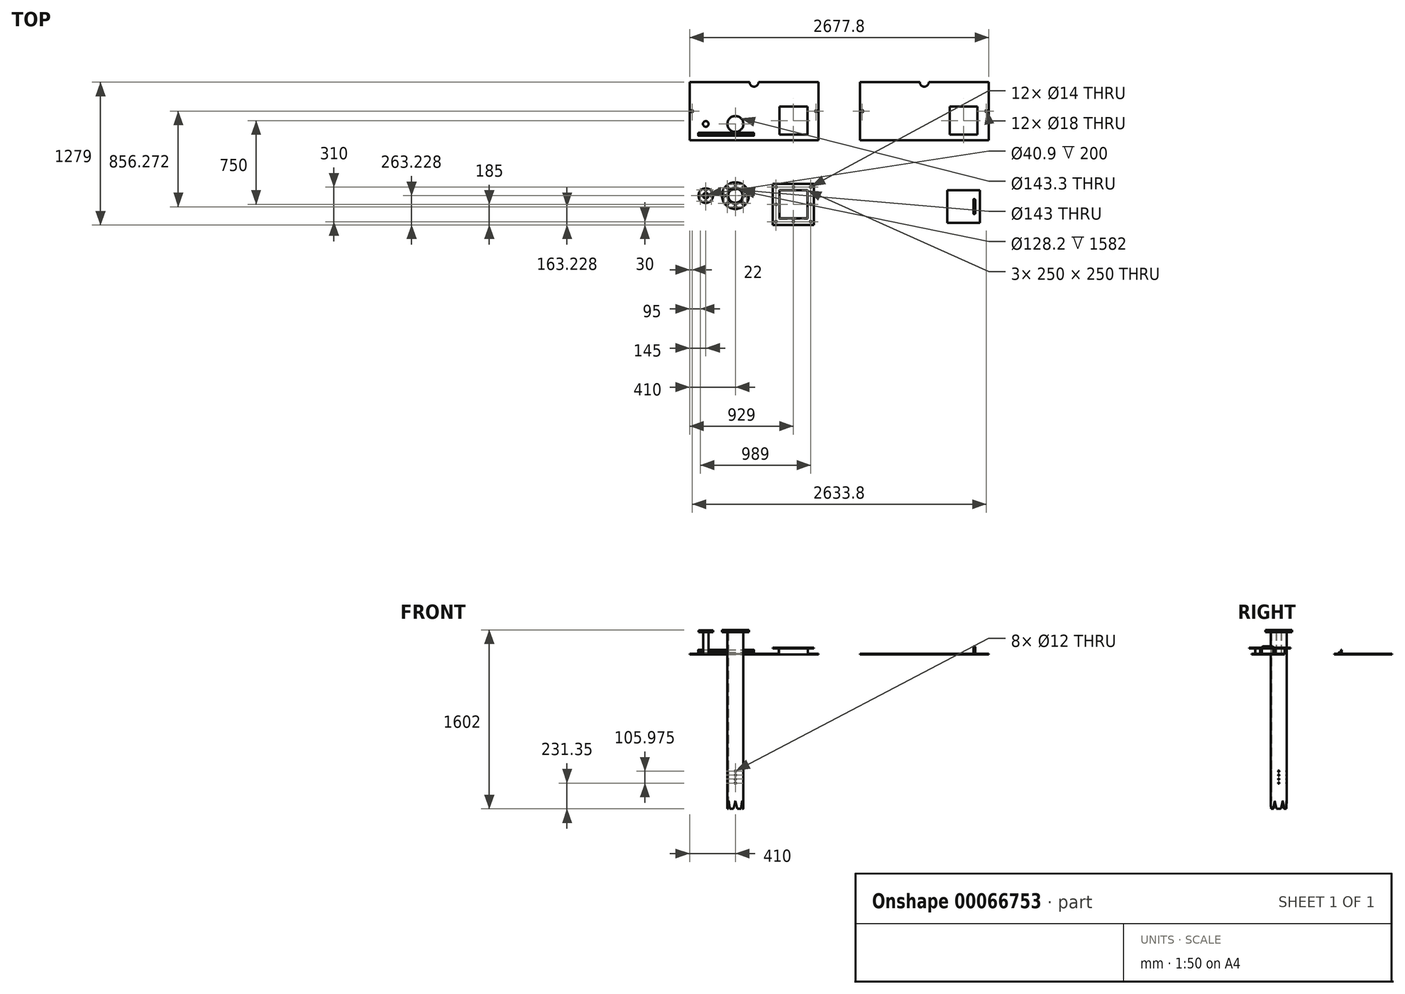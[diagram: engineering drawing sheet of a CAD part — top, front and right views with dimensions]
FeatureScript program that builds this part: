
annotation { "Feature Type Name" : "Feature", "Feature Type Description" : "" }
export const myFeature = defineFeature(function(context is Context, id is Id, definition is map)
    precondition{}
    {
        {
            assignVariable(context, id + "F0", {"name" : "C3", "anyValue" : 6});
        }
        {
            assignVariable(context, id + "F1", {"name" : "C5", "anyValue" : 250});
        }
        {
            assignVariable(context, id + "F2", {"name" : "C7", "anyValue" : 60});
        }
        {
            assignVariable(context, id + "F3", {"name" : "C8", "anyValue" : 6});
        }
        {
            assignVariable(context, id + "F4", {"name" : "C14", "anyValue" : 16});
        }
        {
            assignVariable(context, id + "F5", {"name" : "C16", "anyValue" : 4});
        }
        {
            assignVariable(context, id + "F6", {"name" : "C23", "anyValue" : 20});
        }
        {
            assignVariable(context, id + "F7", {"name" : "C25", "anyValue" : 8});
        }
        {
            var Q0;
            Q0=qCreatedBy(makeId("Top.planeOp"),FACE);
            var sketch = newSketch(context, id + "F8", { "sketchPlane" : qUnion([Q0])});
            skLineSegment(sketch, "E0.bottom", {"start": v(-577, 0) * mm, "end": v(-40, 0) * mm});
            skLineSegment(sketch, "E0.top", {"start": v(-577, -519) * mm, "end": v(577, -519) * mm});
            skLineSegment(sketch, "E0.left", {"start": v(-577, 0) * mm, "end": v(-577, -519) * mm});
            skLineSegment(sketch, "E0.right", {"start": v(577, 0) * mm, "end": v(577, -519) * mm});
            skArc(sketch, "E1", {"start": v(-40, 0) * mm, "mid": v(0, -40) * mm, "end": v(40, 0) * mm});
            skLineSegment(sketch, "E2.trimOffspring", {"start": v(40, 0) * mm, "end": v(577, 0) * mm});
            skCircle(sketch, "E3", {"center": v(-432, -374.1) * mm, "radius": 25.15 * mm});
            skCircle(sketch, "E4", {"center": v(-167, -374.1) * mm, "radius": 71.65 * mm});
            skLineSegment(sketch, "E5.bottom", {"start": v(227, -219) * mm, "end": v(477, -219) * mm});
            skLineSegment(sketch, "E5.top", {"start": v(227, -469) * mm, "end": v(477, -469) * mm});
            skLineSegment(sketch, "E5.left", {"start": v(227, -219) * mm, "end": v(227, -469) * mm});
            skLineSegment(sketch, "E5.right", {"start": v(477, -219) * mm, "end": v(477, -469) * mm});
            skLineSegment(sketch, "E6.bottom", {"start": v(946.8, 0) * mm, "end": v(1483.8, 0) * mm});
            skLineSegment(sketch, "E6.top", {"start": v(946.8, -519) * mm, "end": v(2100.8, -519) * mm});
            skLineSegment(sketch, "E6.left", {"start": v(946.8, 0) * mm, "end": v(946.8, -519) * mm});
            skLineSegment(sketch, "E6.right", {"start": v(2100.8, 0) * mm, "end": v(2100.8, -519) * mm});
            skArc(sketch, "E7", {"start": v(1483.8, 0) * mm, "mid": v(1523.8, -40) * mm, "end": v(1563.8, 0) * mm});
            skLineSegment(sketch, "E8.trimOffspring", {"start": v(1563.8, 0) * mm, "end": v(2100.8, 0) * mm});
            skLineSegment(sketch, "E9.bottom", {"start": v(1750.8, -219) * mm, "end": v(2000.8, -219) * mm});
            skLineSegment(sketch, "E9.top", {"start": v(1750.8, -469) * mm, "end": v(2000.8, -469) * mm});
            skLineSegment(sketch, "E9.left", {"start": v(1750.8, -219) * mm, "end": v(1750.8, -469) * mm});
            skLineSegment(sketch, "E9.right", {"start": v(2000.8, -219) * mm, "end": v(2000.8, -469) * mm});
            skLineSegment(sketch, "E10.bottom", {"start": v(227, -969) * mm, "end": v(477, -969) * mm});
            skLineSegment(sketch, "E10.top", {"start": v(227, -1219) * mm, "end": v(477, -1219) * mm});
            skLineSegment(sketch, "E10.left", {"start": v(227, -969) * mm, "end": v(227, -1219) * mm});
            skLineSegment(sketch, "E10.right", {"start": v(477, -969) * mm, "end": v(477, -1219) * mm});
            skLineSegment(sketch, "E11.bottom", {"start": v(221, -963) * mm, "end": v(483, -963) * mm});
            skLineSegment(sketch, "E11.top", {"start": v(221, -1225) * mm, "end": v(483, -1225) * mm});
            skLineSegment(sketch, "E11.left", {"start": v(221, -963) * mm, "end": v(221, -1225) * mm});
            skLineSegment(sketch, "E11.right", {"start": v(483, -963) * mm, "end": v(483, -1225) * mm});
            skLineSegment(sketch, "E12", {"start": v(352, -469) * mm, "end": v(352, -963) * mm, "construction": true});
            skLineSegment(sketch, "E13", {"start": v(-432, -374.1) * mm, "end": v(-432, -1015.77) * mm, "construction": true});
            skCircle(sketch, "E14", {"center": v(-432, -1015.77) * mm, "radius": 20.45 * mm});
            skCircle(sketch, "E15", {"center": v(-432, -1015.77) * mm, "radius": 24.15 * mm});
            skLineSegment(sketch, "E16", {"start": v(-167, -374.1) * mm, "end": v(-167, -1015.77) * mm, "construction": true});
            skCircle(sketch, "E17", {"center": v(-167, -1015.77) * mm, "radius": 64.1 * mm});
            skCircle(sketch, "E18", {"center": v(-167, -1015.77) * mm, "radius": 70.65 * mm});
            skLineSegment(sketch, "E19", {"start": v(1875.8, -469) * mm, "end": v(1875.8, -969) * mm, "construction": true});
            skLineSegment(sketch, "E20.bottom", {"start": v(1730.8, -969) * mm, "end": v(2020.8, -969) * mm});
            skLineSegment(sketch, "E20.top", {"start": v(1730.8, -1259) * mm, "end": v(2020.8, -1259) * mm});
            skLineSegment(sketch, "E20.left", {"start": v(1730.8, -969) * mm, "end": v(1730.8, -1259) * mm});
            skLineSegment(sketch, "E20.right", {"start": v(2020.8, -969) * mm, "end": v(2020.8, -1259) * mm});
            skCircle(sketch, "E21", {"center": v(555, -259.5) * mm, "radius": 9 * mm});
            skLineSegment(sketch, "E22", {"start": v(555, -259.5) * mm, "end": v(577, -259.5) * mm, "construction": true});
            skCircle(sketch, "E23.MirrorC", {"center": v(-555, -259.5) * mm, "radius": 9 * mm});
            skLineSegment(sketch, "E24", {"start": v(946.8, -259.5) * mm, "end": v(968.8, -259.5) * mm, "construction": true});
            skCircle(sketch, "E25", {"center": v(968.8, -259.5) * mm, "radius": 9 * mm});
            skLineSegment(sketch, "E26", {"start": v(1523.8, 0) * mm, "end": v(1523.8, -89.88) * mm, "construction": true});
            skCircle(sketch, "E27.MirrorC", {"center": v(2078.8, -259.5) * mm, "radius": 9 * mm});
            skSolve(sketch);
        }
        {
            var Q0;
            Q0=makeQuery(id+"F8.imprint","IMPRINT",FACE,{"disambiguationData":[TD([[makeQuery(id+"F8.imprint","IMPRINT",EDGE,{"derivedFrom":sQuery(id+"F8.wireOp",EDGE,"E0.bottom")}),-1.0]])]});
            extrude(context, id + "F9", {"entities" : qUnion([Q0]), "depth" : (getVariable(context, 'C3')) * mm});
        }
        {
            var Q0;
            Q0=makeQuery(id+"F8.imprint","IMPRINT",FACE,{"disambiguationData":[TD([[makeQuery(id+"F8.imprint","IMPRINT",EDGE,{"derivedFrom":sQuery(id+"F8.wireOp",EDGE,"E10.bottom")}),1.0]])]});
            extrude(context, id + "F10", {"entities" : qUnion([Q0]), "depth" : (getVariable(context, 'C7')) * mm});
        }
        {
            var Q0;
            Q0=makeQuery(id+"F10.opExtrude","CAP_FACE",FACE,{"disambiguationData":[OSD([sQuery(id+"F8.wireOp",EDGE,"E10.bottom"),sQuery(id+"F8.wireOp",EDGE,"E10.top"),sQuery(id+"F8.wireOp",EDGE,"E10.left"),sQuery(id+"F8.wireOp",EDGE,"E10.right"),sQuery(id+"F8.wireOp",EDGE,"E11.bottom"),sQuery(id+"F8.wireOp",EDGE,"E11.top"),sQuery(id+"F8.wireOp",EDGE,"E11.left"),sQuery(id+"F8.wireOp",EDGE,"E11.right")])],"isStart":false});
            var sketch = newSketch(context, id + "F11", { "sketchPlane" : qUnion([Q0])});
            skLineSegment(sketch, "E28.bottom", {"start": v(167, -909) * mm, "end": v(537, -909) * mm});
            skLineSegment(sketch, "E28.top", {"start": v(167, -1279) * mm, "end": v(537, -1279) * mm});
            skLineSegment(sketch, "E28.left", {"start": v(167, -909) * mm, "end": v(167, -1279) * mm});
            skLineSegment(sketch, "E28.right", {"start": v(537, -909) * mm, "end": v(537, -1279) * mm});
            skLineSegment(sketch, "E29.bottom", {"start": v(227, -969) * mm, "end": v(477, -969) * mm});
            skLineSegment(sketch, "E29.top", {"start": v(227, -1219) * mm, "end": v(477, -1219) * mm});
            skLineSegment(sketch, "E29.left", {"start": v(227, -969) * mm, "end": v(227, -1219) * mm});
            skLineSegment(sketch, "E29.right", {"start": v(477, -969) * mm, "end": v(477, -1219) * mm});
            skLineSegment(sketch, "E30.bottom", {"start": v(197, -939) * mm, "end": v(507, -939) * mm, "construction": true});
            skLineSegment(sketch, "E30.top", {"start": v(197, -1249) * mm, "end": v(507, -1249) * mm, "construction": true});
            skLineSegment(sketch, "E30.left", {"start": v(197, -939) * mm, "end": v(197, -1249) * mm, "construction": true});
            skLineSegment(sketch, "E30.right", {"start": v(507, -939) * mm, "end": v(507, -1249) * mm, "construction": true});
            skCircle(sketch, "E31", {"center": v(197, -939) * mm, "radius": 7 * mm});
            skCircle(sketch, "E32", {"center": v(507, -939) * mm, "radius": 7 * mm});
            skCircle(sketch, "E33", {"center": v(352, -939) * mm, "radius": 7 * mm});
            skCircle(sketch, "E34", {"center": v(197, -1094) * mm, "radius": 7 * mm});
            skCircle(sketch, "E35", {"center": v(197, -1249) * mm, "radius": 7 * mm});
            skCircle(sketch, "E36", {"center": v(352, -1249) * mm, "radius": 7 * mm});
            skCircle(sketch, "E37", {"center": v(507, -1249) * mm, "radius": 7 * mm});
            skCircle(sketch, "E38", {"center": v(507, -1094) * mm, "radius": 7 * mm});
            skSolve(sketch);
        }
        {
            var Q0;
            Q0=makeQuery(id+"F11.imprint","IMPRINT",FACE,{"disambiguationData":[TD([[makeQuery(id+"F11.imprint","IMPRINT",EDGE,{"derivedFrom":sQuery(id+"F11.wireOp",EDGE,"E28.bottom")}),-1.0]])]});
            extrude(context, id + "F12", {"entities" : qUnion([Q0]), "operationType" : NewBodyOperationType.ADD, "oppositeDirection" : true, "depth" : (getVariable(context, 'C8')) * mm});
        }
        {
            var Q0;
            Q0=makeQuery(id+"F8.imprint","IMPRINT",FACE,{"disambiguationData":[TD([[makeQuery(id+"F8.imprint","IMPRINT",EDGE,{"derivedFrom":sQuery(id+"F8.wireOp",EDGE,"E14")}),-1.0]])]});
            extrude(context, id + "F13", {"entities" : qUnion([Q0]), "depth" : 200 * mm});
        }
        {
            var Q0;
            Q0=makeQuery(id+"F13.opExtrude","CAP_FACE",FACE,{"disambiguationData":[OSD([sQuery(id+"F8.wireOp",EDGE,"E14"),sQuery(id+"F8.wireOp",EDGE,"E15")])],"isStart":false});
            var sketch = newSketch(context, id + "F14", { "sketchPlane" : qUnion([Q0])});
            skCircle(sketch, "E39", {"center": v(-432, -1015.77) * mm, "radius": 24.75 * mm});
            skCircle(sketch, "E40", {"center": v(-432, -1015.77) * mm, "radius": 65 * mm});
            skCircle(sketch, "E41", {"center": v(-432, -1015.77) * mm, "radius": 50 * mm, "construction": true});
            skCircle(sketch, "E42", {"center": v(-432, -965.77) * mm, "radius": 7 * mm});
            skSolve(sketch);
        }
        {
            var Q0;
            Q0=makeQuery(id+"F14.imprint","IMPRINT",FACE,{"disambiguationData":[TD([[makeQuery(id+"F14.imprint","IMPRINT",EDGE,{"derivedFrom":sQuery(id+"F14.wireOp",EDGE,"E39")}),-1.0]])]});
            extrude(context, id + "F15", {"entities" : qUnion([Q0]), "depth" : (getVariable(context, 'C14')) * mm});
        }
        {
            var Q0;
            Q0=makeQuery(id+"F15.opExtrude","SWEPT_FACE",FACE,{"disambiguationData":[OSD([sQuery(id+"F14.wireOp",EDGE,"E42")])]});
            var Q1;
            Q1=makeQuery(id+"F15.opExtrude","CAP_EDGE",EDGE,{"disambiguationData":[OSD([sQuery(id+"F14.wireOp",EDGE,"E39")])],"isStart":false});
            circularPattern(context, id + "F16", {"faces" : qUnion([Q0]), "axis" : qUnion([Q1]), "angle" : 360 * degree, "instanceCount" : getVariable(context, 'C16'), "equalSpace" : true, "patternType" : PatternType.FACE});
        }
        {
            assignVariable(context, id + "F17", {"name" : "C29", "anyValue" : 1382});
        }
        {
            var Q0;
            Q0=makeQuery(id+"F8.imprint","IMPRINT",FACE,{"disambiguationData":[TD([[makeQuery(id+"F8.imprint","IMPRINT",EDGE,{"derivedFrom":sQuery(id+"F8.wireOp",EDGE,"E17")}),-1.0]])]});
            extrude(context, id + "F18", {"entities" : qUnion([Q0]), "depth" : 200 * mm, "hasSecondDirection" : true, "secondDirectionOppositeDirection" : true, "secondDirectionDepth" : (getVariable(context, 'C29')) * mm});
        }
        {
            var Q0;
            Q0=makeQuery(id+"F18.opExtrude","CAP_FACE",FACE,{"disambiguationData":[OSD([sQuery(id+"F8.wireOp",EDGE,"E17"),sQuery(id+"F8.wireOp",EDGE,"E18")])],"isStart":false});
            var sketch = newSketch(context, id + "F19", { "sketchPlane" : qUnion([Q0])});
            skCircle(sketch, "E43", {"center": v(-167, -1015.77) * mm, "radius": 71.5 * mm});
            skCircle(sketch, "E44", {"center": v(-167, -1015.77) * mm, "radius": 120 * mm});
            skCircle(sketch, "E45", {"center": v(-167, -1015.77) * mm, "radius": 100 * mm, "construction": true});
            skCircle(sketch, "E46", {"center": v(-167, -915.77) * mm, "radius": 9 * mm});
            skSolve(sketch);
        }
        {
            var Q0;
            Q0=makeQuery(id+"F19.imprint","IMPRINT",FACE,{"disambiguationData":[TD([[makeQuery(id+"F19.imprint","IMPRINT",EDGE,{"derivedFrom":sQuery(id+"F19.wireOp",EDGE,"E43")}),-1.0]])]});
            extrude(context, id + "F20", {"entities" : qUnion([Q0]), "depth" : (getVariable(context, 'C23')) * mm});
        }
        {
            var Q0;
            Q0=makeQuery(id+"F20.opExtrude","SWEPT_FACE",FACE,{"disambiguationData":[OSD([sQuery(id+"F19.wireOp",EDGE,"E46")])]});
            var Q1;
            Q1=makeQuery(id+"F20.opExtrude","CAP_EDGE",EDGE,{"disambiguationData":[OSD([sQuery(id+"F19.wireOp",EDGE,"E43")])],"isStart":false});
            circularPattern(context, id + "F21", {"faces" : qUnion([Q0]), "axis" : qUnion([Q1]), "angle" : 360 * degree, "instanceCount" : getVariable(context, 'C25'), "equalSpace" : true, "patternType" : PatternType.FACE});
        }
        {
            var Q0;
            Q0=makeQuery(id+"F8.imprint","IMPRINT",FACE,{"disambiguationData":[TD([[makeQuery(id+"F8.imprint","IMPRINT",EDGE,{"derivedFrom":sQuery(id+"F8.wireOp",EDGE,"E6.bottom")}),-1.0]])]});
            extrude(context, id + "F22", {"entities" : qUnion([Q0]), "depth" : (getVariable(context, 'C3')) * mm});
        }
        {
            var Q0;
            Q0=makeQuery(id+"F8.imprint","IMPRINT",FACE,{"disambiguationData":[TD([[makeQuery(id+"F8.imprint","IMPRINT",EDGE,{"derivedFrom":sQuery(id+"F8.wireOp",EDGE,"E20.bottom")}),-1.0]])]});
            extrude(context, id + "F23", {"entities" : qUnion([Q0]), "depth" : (getVariable(context, 'C8')) * mm});
        }
        {
            var Q0;
            Q0=qCreatedBy(makeId("Right.planeOp"),FACE);
            var sketch = newSketch(context, id + "F24", { "sketchPlane" : qUnion([Q0])});
            skLineSegment(sketch, "E47", {"start": v(-478.36, 15.27) * mm, "end": v(-453.36, 15.27) * mm});
            skLineSegment(sketch, "E48", {"start": v(-453.36, 15.27) * mm, "end": v(-453.36, 40.27) * mm});
            skLineSegment(sketch, "E49", {"start": v(-453.36, 40.27) * mm, "end": v(-456.36, 40.27) * mm});
            skLineSegment(sketch, "E50", {"start": v(-458.36, 38.27) * mm, "end": v(-458.36, 23.77) * mm});
            skLineSegment(sketch, "E51", {"start": v(-461.86, 20.27) * mm, "end": v(-476.36, 20.27) * mm});
            skLineSegment(sketch, "E52", {"start": v(-478.36, 18.27) * mm, "end": v(-478.36, 15.27) * mm});
            skPoint(sketch, "E53.visualSharp", {"position": v(-458.36, 20.27) * mm});
            skArc(sketch, "E53.filletArc", {"start": v(-461.86, 20.27) * mm, "mid": v(-459.38, 21.3) * mm, "end": v(-458.36, 23.77) * mm});
            skPoint(sketch, "E54.visualSharp", {"position": v(-458.36, 40.27) * mm});
            skArc(sketch, "E54.filletArc", {"start": v(-456.36, 40.27) * mm, "mid": v(-457.77, 39.69) * mm, "end": v(-458.36, 38.27) * mm});
            skPoint(sketch, "E55.visualSharp", {"position": v(-478.36, 20.27) * mm});
            skArc(sketch, "E55.filletArc", {"start": v(-476.36, 20.27) * mm, "mid": v(-477.77, 19.69) * mm, "end": v(-478.36, 18.27) * mm});
            skSolve(sketch);
        }
        {
            var Q0;
            Q0=makeQuery(id+"F24.imprint","IMPRINT",FACE,{"disambiguationData":[TD([[makeQuery(id+"F24.imprint","IMPRINT",EDGE,{"derivedFrom":sQuery(id+"F24.wireOp",EDGE,"E47")}),1.0]])]});
            extrude(context, id + "F25", {"entities" : qUnion([Q0]), "oppositeDirection" : true, "depth" : (2 * getVariable(context, 'C5')) * mm});
        }
        {
            var Q0;
            Q0=makeQuery(id+"F23.opExtrude","CAP_FACE",FACE,{"disambiguationData":[OSD([sQuery(id+"F8.wireOp",EDGE,"E20.bottom"),sQuery(id+"F8.wireOp",EDGE,"E20.top"),sQuery(id+"F8.wireOp",EDGE,"E20.left"),sQuery(id+"F8.wireOp",EDGE,"E20.right")])],"isStart":false});
            var sketch = newSketch(context, id + "F26", { "sketchPlane" : qUnion([Q0])});
            skCircle(sketch, "E56", {"center": v(1970.8, -1174) * mm, "radius": 8 * mm});
            skLineSegment(sketch, "E57", {"start": v(2020.8, -1114) * mm, "end": v(1796.76, -1114) * mm, "construction": true});
            skLineSegment(sketch, "E58", {"start": v(1970.8, -1174) * mm, "end": v(2020.8, -1174) * mm, "construction": true});
            skSolve(sketch);
        }
        {
            var Q0;
            Q0=makeQuery(id+"F23.opExtrude","SWEPT_FACE",FACE,{"disambiguationData":[OSD([sQuery(id+"F8.wireOp",EDGE,"E20.right")])]});
            var sketch = newSketch(context, id + "F27", { "sketchPlane" : qUnion([Q0])});
            skLineSegment(sketch, "E59", {"start": v(-1174, 6) * mm, "end": v(-1174, 36) * mm});
            skLineSegment(sketch, "E60", {"start": v(-1144, 66) * mm, "end": v(-1084, 66) * mm});
            skLineSegment(sketch, "E61", {"start": v(-1054, 36) * mm, "end": v(-1054, 6) * mm});
            skPoint(sketch, "E62.visualSharp", {"position": v(-1174, 66) * mm});
            skArc(sketch, "E62.filletArc", {"start": v(-1144, 66) * mm, "mid": v(-1165.21, 57.21) * mm, "end": v(-1174, 36) * mm});
            skPoint(sketch, "E63.visualSharp", {"position": v(-1054, 66) * mm});
            skArc(sketch, "E63.filletArc", {"start": v(-1054, 36) * mm, "mid": v(-1062.79, 57.21) * mm, "end": v(-1084, 66) * mm});
            skSolve(sketch);
        }
        {
            var Q0;
            Q0=makeQuery(id+"F26.imprint","IMPRINT",FACE,{"disambiguationData":[TD([[makeQuery(id+"F26.imprint","IMPRINT",EDGE,{"derivedFrom":sQuery(id+"F26.wireOp",EDGE,"E56")}),1.0]])]});
            var Q1;
            Q1=sQuery(id+"F27.wireOp",EDGE,"E59");
            var Q2;
            Q2=sQuery(id+"F27.wireOp",EDGE,"E62.filletArc");
            var Q3;
            Q3=sQuery(id+"F27.wireOp",EDGE,"E60");
            var Q4;
            Q4=sQuery(id+"F27.wireOp",EDGE,"E63.filletArc");
            var Q5;
            Q5=sQuery(id+"F27.wireOp",EDGE,"E61");
            sweep(context, id + "F28", {"operationType" : NewBodyOperationType.ADD, "profiles" : qUnion([Q0]), "path" : qUnion([Q1, Q2, Q3, Q4, Q5])});
        }
        {
            var Q0;
            Q0=sQuery(id+"F8.wireOp",VERTEX,"E18.center");
            var Q1;
            Q1=sQuery(id+"F8.wireOp",EDGE,"E16");
            cPlane(context, id + "F29", {"entities" : qUnion([Q0, Q1]), "cplaneType" : CPlaneType.LINE_POINT, "offset" : 150 * mm, "width" : 150 * mm, "height" : 150 * mm});
        }
        {
            assignVariable(context, id + "F30", {"name" : "C28", "anyValue" : 4});
        }
        {
            var Q0;
            Q0=qCreatedBy(id+"F29.planeOp",FACE);
            var sketch = newSketch(context, id + "F31", { "sketchPlane" : qUnion([Q0])});
            skLineSegment(sketch, "E64", {"start": v(-184.66, -1382) * mm, "end": v(-167, -1311.35) * mm});
            skLineSegment(sketch, "E65", {"start": v(-167, -1311.35) * mm, "end": v(-149.34, -1382) * mm});
            skLineSegment(sketch, "E66", {"start": v(-149.34, -1382) * mm, "end": v(-184.66, -1382) * mm});
            skCircle(sketch, "E67", {"center": v(-167, -1150.65) * mm, "radius": 6 * mm});
            skCircle(sketch, "E68", {"center": v(-167, -1115.33) * mm, "radius": 6 * mm});
            skLineSegment(sketch, "E69", {"start": v(-167, -1150.65) * mm, "end": v(-167, -1115.33) * mm, "construction": true});
            skLineSegment(sketch, "E70", {"start": v(-167, -1115.33) * mm, "end": v(-167, -1080) * mm, "construction": true});
            skLineSegment(sketch, "E71", {"start": v(-167, -1080) * mm, "end": v(-167, -1044.67) * mm, "construction": true});
            skLineSegment(sketch, "E72.trimOffspring", {"start": v(-167, -1311.35) * mm, "end": v(-167, -1382) * mm, "construction": true});
            skCircle(sketch, "E73", {"center": v(-167, -1080) * mm, "radius": 6 * mm});
            skCircle(sketch, "E74", {"center": v(-167, -1044.67) * mm, "radius": 6 * mm});
            skSolve(sketch);
        }
        {
            var Q0;
            Q0=makeQuery(id+"F31.imprint","IMPRINT",FACE,{"disambiguationData":[TD([[makeQuery(id+"F31.imprint","IMPRINT",EDGE,{"derivedFrom":sQuery(id+"F31.wireOp",EDGE,"E64")}),-1.0]])]});
            extrude(context, id + "F32", {"entities" : qUnion([Q0]), "operationType" : NewBodyOperationType.REMOVE, "endBound" : BoundingType.THROUGH_ALL, "depth" : 25 * mm});
        }
        {
            var Q0;
            Q0=makeQuery(id+"F32.boolean.opBoolean","COPY",FACE,{"derivedFrom":makeQuery(id+"F32.opExtrude","SWEPT_FACE",FACE,{"disambiguationData":[OSD([sQuery(id+"F31.wireOp",EDGE,"E64")])]})});
            var Q1;
            Q1=makeQuery(id+"F32.boolean.opBoolean","COPY",FACE,{"derivedFrom":makeQuery(id+"F32.opExtrude","SWEPT_FACE",FACE,{"disambiguationData":[OSD([sQuery(id+"F31.wireOp",EDGE,"E65")])]})});
            var Q2;
            Q2=makeQuery(id+"F18.opExtrude","SWEPT_FACE",FACE,{"disambiguationData":[OSD([sQuery(id+"F8.wireOp",EDGE,"E17")])]});
            circularPattern(context, id + "F33", {"faces" : qUnion([Q0, Q1]), "axis" : qUnion([Q2]), "angle" : 360 * degree, "instanceCount" : 6, "equalSpace" : true, "patternType" : PatternType.FACE});
        }
        {
            var Q0;
            Q0 = qSketchRegion(id + "F31", true);
            extrude(context, id + "F34", {"entities" : qUnion([Q0]), "operationType" : NewBodyOperationType.REMOVE, "endBound" : BoundingType.THROUGH_ALL, "depth" : 25 * mm});
        }
        {
            var Q0;
            Q0=makeQuery(id+"F34.boolean.opBoolean","COPY",FACE,{"derivedFrom":makeQuery(id+"F34.opExtrude","SWEPT_FACE",FACE,{"disambiguationData":[OSD([sQuery(id+"F31.wireOp",EDGE,"E67")])]})});
            var Q1;
            Q1=makeQuery(id+"F34.boolean.opBoolean","COPY",FACE,{"derivedFrom":makeQuery(id+"F34.opExtrude","SWEPT_FACE",FACE,{"disambiguationData":[OSD([sQuery(id+"F31.wireOp",EDGE,"E68")])]})});
            var Q2;
            Q2=makeQuery(id+"F34.boolean.opBoolean","COPY",FACE,{"derivedFrom":makeQuery(id+"F34.opExtrude","SWEPT_FACE",FACE,{"disambiguationData":[OSD([sQuery(id+"F31.wireOp",EDGE,"E73")])]})});
            var Q3;
            Q3=makeQuery(id+"F34.boolean.opBoolean","COPY",FACE,{"derivedFrom":makeQuery(id+"F34.opExtrude","SWEPT_FACE",FACE,{"disambiguationData":[OSD([sQuery(id+"F31.wireOp",EDGE,"E74")])]})});
            var Q4;
            Q4=sQuery(id+"F31.wireOp",EDGE,"E72.trimOffspring");
            circularPattern(context, id + "F35", {"patternType" : PatternType.FACE, "faces" : qUnion([Q0, Q1, Q2, Q3]), "axis" : qUnion([Q4]), "angle" : 360 * degree, "instanceCount" : getVariable(context, 'C28'), "equalSpace" : true});
        }
    });
